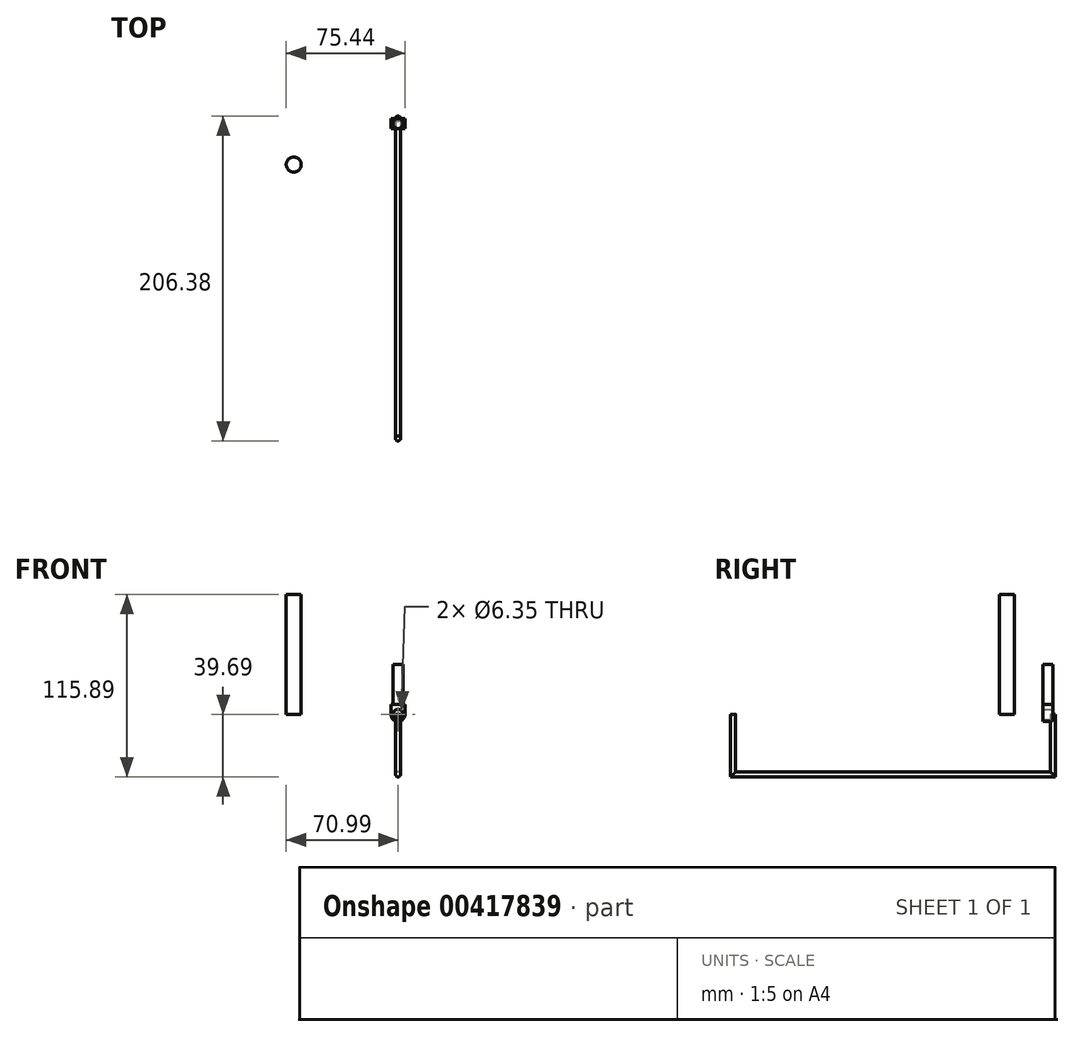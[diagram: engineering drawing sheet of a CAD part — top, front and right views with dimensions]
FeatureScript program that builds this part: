
annotation { "Feature Type Name" : "Feature", "Feature Type Description" : "" }
export const myFeature = defineFeature(function(context is Context, id is Id, definition is map)
    precondition{}
    {
        {
            var Q0;
            Q0=qCreatedBy(makeId("Front.planeOp"),FACE);
            var sketch = newSketch(context, id + "F0", { "sketchPlane" : qUnion([Q0])});
            skCircle(sketch, "E0", {"center": v(0, 0) * mm, "radius": 3.17 * mm});
            skCircle(sketch, "E1", {"center": v(0, 0) * mm, "radius": 4.45 * mm});
            skLineSegment(sketch, "E2", {"start": v(-4.45, 0) * mm, "end": v(-4.45, 6.35) * mm});
            skLineSegment(sketch, "E3", {"start": v(4.45, 0) * mm, "end": v(4.45, 6.35) * mm});
            skLineSegment(sketch, "E4", {"start": v(4.45, 6.35) * mm, "end": v(-4.45, 6.35) * mm});
            skSolve(sketch);
        }
        {
            var Q0;
            {var subQ0=sQuery(id+"F0.wireOp",EDGE,"E2");Q0=makeQuery(id+"F0.imprint","IMPRINT",FACE,{"disambiguationData":[TD([[makeQuery(id+"F0.imprint","IMPRINT",EDGE,{"derivedFrom":subQ0}),-1.0]])]});}
            var Q1;
            Q1=makeQuery(id+"F0.imprint","IMPRINT",FACE,{"disambiguationData":[TD([[makeQuery(id+"F0.imprint","IMPRINT",EDGE,{"derivedFrom":sQuery(id+"F0.wireOp",EDGE,"E0")}),-1.0]])]});
            extrude(context, id + "F1", {"entities" : qUnion([Q0, Q1]), "depth" : 6.35 * mm});
        }
        {
            var Q0;
            Q0=makeQuery(id+"F1.opExtrude","SWEPT_FACE",FACE,{"disambiguationData":[OSD([sQuery(id+"F0.wireOp",EDGE,"E4")])]});
            var sketch = newSketch(context, id + "F2", { "sketchPlane" : qUnion([Q0])});
            skCircle(sketch, "E5", {"center": v(0, -3.18) * mm, "radius": 3.18 * mm});
            skPoint(sketch, "E5.centerSnap0", {"position": v(-4.45, -3.18) * mm});
            skSolve(sketch);
        }
        {
            var Q0;
            {var subQ0=sQuery(id+"F2.wireOp",EDGE,"E5");var subQ1=sQuery(id+"F0.wireOp",EDGE,"E4");var subQ2=makeQuery(id+"F2.imprint","INTERSECT",VERTEX,{"derivedFrom":[makeQuery(id+"F1.opExtrude","CAP_EDGE",EDGE,{"disambiguationData":[OSD([subQ1])],"isStart":true}),subQ0]});Q0=makeQuery(id+"F2.imprint","IMPRINT",FACE,{"disambiguationData":[TD([[makeQuery(id+"F2.imprint","IMPRINT",EDGE,{"disambiguationData":[TD([[subQ2,-1.0]])],"derivedFrom":subQ0}),1.0]])]});}
            extrude(context, id + "F3", {"entities" : qUnion([Q0]), "depth" : 25.4 * mm});
        }
        {
            var Q0;
            Q0=qCreatedBy(makeId("Right.planeOp"),FACE);
            var sketch = newSketch(context, id + "F4", { "sketchPlane" : qUnion([Q0])});
            skLineSegment(sketch, "E6", {"start": v(0, 0) * mm, "end": v(0, -38.1) * mm});
            skLineSegment(sketch, "E7", {"start": v(0, -38.1) * mm, "end": v(-203.2, -38.1) * mm});
            skLineSegment(sketch, "E8", {"start": v(-203.2, -38.1) * mm, "end": v(-203.2, 0) * mm});
            skSolve(sketch);
        }
        {
            var Q0;
            Q0=qCreatedBy(makeId("Top.planeOp"),FACE);
            var sketch = newSketch(context, id + "F5", { "sketchPlane" : qUnion([Q0])});
            skCircle(sketch, "E9", {"center": v(0, 0) * mm, "radius": 1.59 * mm});
            skSolve(sketch);
        }
        {
            var Q0;
            Q0=makeQuery(id+"F5.imprint","IMPRINT",FACE,{"disambiguationData":[TD([[makeQuery(id+"F5.imprint","IMPRINT",EDGE,{"derivedFrom":sQuery(id+"F5.wireOp",EDGE,"E9")}),1.0]])]});
            var Q1;
            Q1=sQuery(id+"F4.wireOp",EDGE,"E6");
            var Q2;
            Q2=sQuery(id+"F4.wireOp",EDGE,"E7");
            var Q3;
            Q3=sQuery(id+"F4.wireOp",EDGE,"E8");
            sweep(context, id + "F6", {"profiles" : qUnion([Q0]), "path" : qUnion([Q1, Q2, Q3])});
        }
        {
            var Q0;
            Q0=qCreatedBy(makeId("Top.planeOp"),FACE);
            var sketch = newSketch(context, id + "F7", { "sketchPlane" : qUnion([Q0])});
            skCircle(sketch, "E10", {"center": v(-66.22, -29.24) * mm, "radius": 4.76 * mm});
            skSolve(sketch);
        }
        {
            var Q0;
            Q0=makeQuery(id+"F7.imprint","IMPRINT",FACE,{"disambiguationData":[TD([[makeQuery(id+"F7.imprint","IMPRINT",EDGE,{"derivedFrom":sQuery(id+"F7.wireOp",EDGE,"E10")}),1.0]])]});
            extrude(context, id + "F8", {"entities" : qUnion([Q0]), "depth" : 76.2 * mm});
        }
    });
